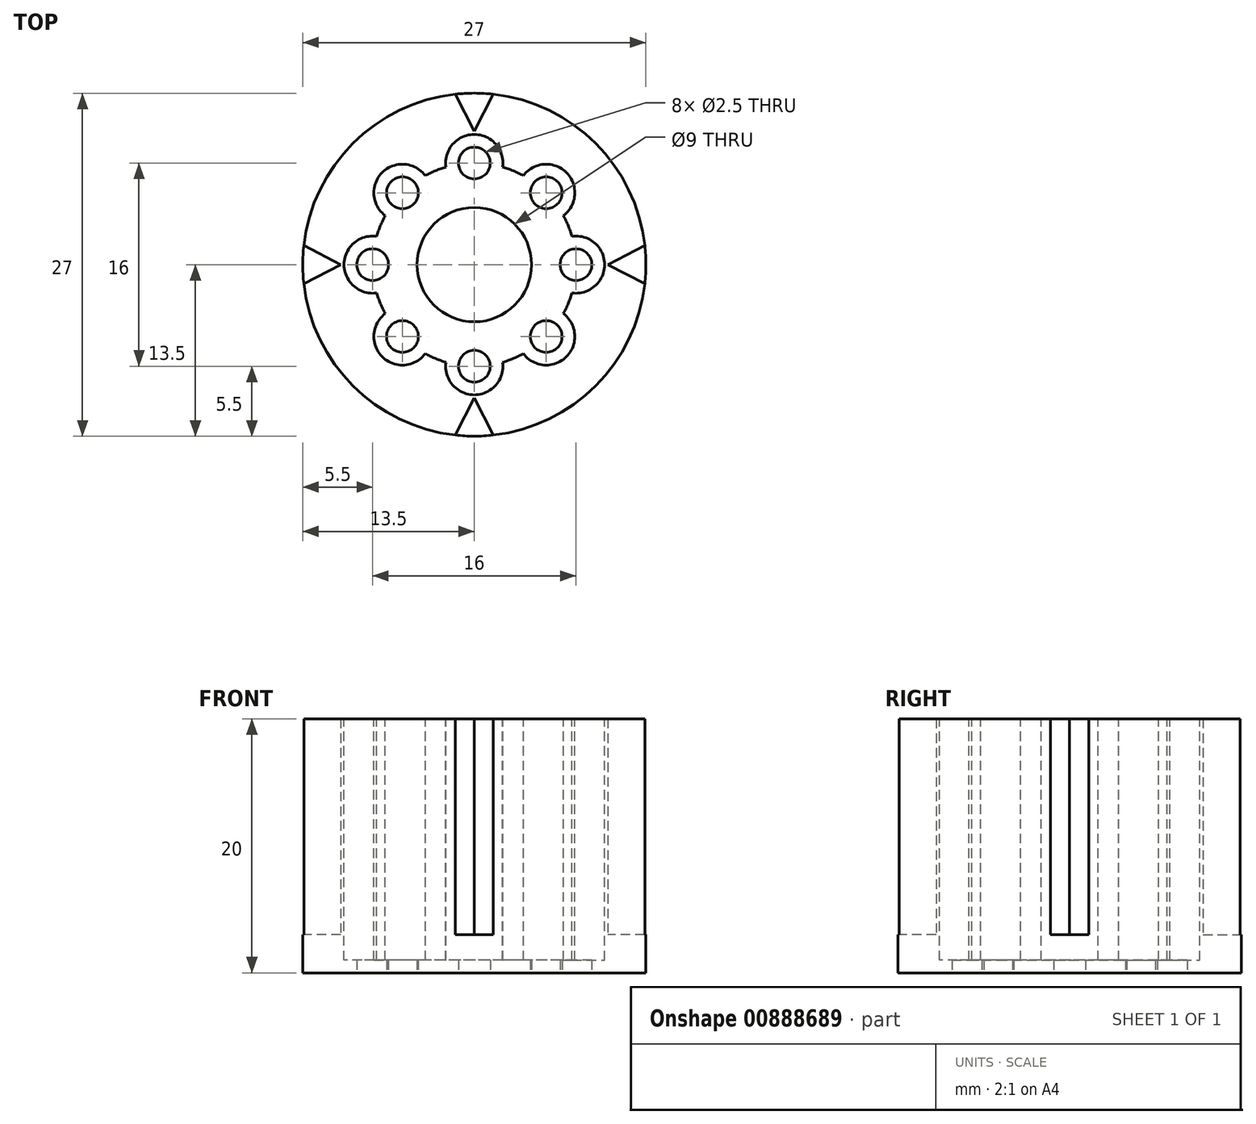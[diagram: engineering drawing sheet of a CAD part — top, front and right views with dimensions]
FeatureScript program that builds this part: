
annotation { "Feature Type Name" : "Feature", "Feature Type Description" : "" }
export const myFeature = defineFeature(function(context is Context, id is Id, definition is map)
    precondition{}
    {
        {
            var Q0;
            Q0=qCreatedBy(makeId("Top.planeOp"),FACE);
            var sketch = newSketch(context, id + "F0", { "sketchPlane" : qUnion([Q0])});
            skArc(sketch, "E0", {"start": v(-13.42, -1.5) * mm, "mid": v(-9.55, -9.55) * mm, "end": v(-1.5, -13.42) * mm});
            skLineSegment(sketch, "E1", {"start": v(-1.5, 13.42) * mm, "end": v(0, 10.5) * mm});
            skLineSegment(sketch, "E2", {"start": v(0, 10.5) * mm, "end": v(1.5, 13.42) * mm});
            skCircle(sketch, "E3", {"center": v(0, 0) * mm, "radius": 10.5 * mm, "construction": true});
            skLineSegment(sketch, "E4", {"start": v(-13.42, 1.5) * mm, "end": v(-10.5, 0) * mm});
            skLineSegment(sketch, "E5", {"start": v(-1.5, -13.42) * mm, "end": v(0, -10.5) * mm});
            skLineSegment(sketch, "E6", {"start": v(13.42, 1.5) * mm, "end": v(10.5, 0) * mm});
            skLineSegment(sketch, "E7", {"start": v(10.5, 0) * mm, "end": v(13.42, -1.5) * mm});
            skLineSegment(sketch, "E8", {"start": v(-10.5, 0) * mm, "end": v(-13.42, -1.5) * mm});
            skLineSegment(sketch, "E9", {"start": v(0, -10.5) * mm, "end": v(1.5, -13.42) * mm});
            skArc(sketch, "E10.trimOffspring", {"start": v(-1.5, 13.42) * mm, "mid": v(-9.55, 9.55) * mm, "end": v(-13.42, 1.5) * mm});
            skArc(sketch, "E11.trimOffspring", {"start": v(13.42, 1.5) * mm, "mid": v(9.55, 9.55) * mm, "end": v(1.5, 13.42) * mm});
            skArc(sketch, "E12.trimOffspring", {"start": v(1.5, -13.42) * mm, "mid": v(9.55, -9.55) * mm, "end": v(13.42, -1.5) * mm});
            skCircle(sketch, "E13", {"center": v(0, 0) * mm, "radius": 4.5 * mm});
            skCircle(sketch, "E14", {"center": v(0, 0) * mm, "radius": 8 * mm, "construction": true});
            skCircle(sketch, "E15", {"center": v(-8, 0) * mm, "radius": 1.25 * mm});
            skCircle(sketch, "E16", {"center": v(0, 8) * mm, "radius": 1.25 * mm});
            skCircle(sketch, "E17", {"center": v(8, 0) * mm, "radius": 1.25 * mm});
            skCircle(sketch, "E18", {"center": v(0, -8) * mm, "radius": 1.25 * mm});
            skCircle(sketch, "E19", {"center": v(-5.66, 5.66) * mm, "radius": 1.25 * mm});
            skCircle(sketch, "E20", {"center": v(5.66, 5.66) * mm, "radius": 1.25 * mm});
            skCircle(sketch, "E21", {"center": v(5.66, -5.66) * mm, "radius": 1.25 * mm});
            skCircle(sketch, "E22", {"center": v(-5.66, -5.66) * mm, "radius": 1.25 * mm});
            skLineSegment(sketch, "E23", {"start": v(-16.79, -16.79) * mm, "end": v(17, 17) * mm, "construction": true});
            skLineSegment(sketch, "E24", {"start": v(-15.4, 15.4) * mm, "end": v(13.72, -13.72) * mm, "construction": true});
            skSolve(sketch);
        }
        {
            var Q0;
            Q0 = qSketchRegion(id + "F0", true);
            extrude(context, id + "F1", {"entities" : qUnion([Q0]), "depth" : 20 * mm, "offsetDistance" : 25 * mm});
        }
        {
            var Q0;
            Q0=makeQuery(id+"F1.opExtrude","CAP_FACE",FACE,{"disambiguationData":[OSD([sQuery(id+"F0.wireOp",EDGE,"E0"),sQuery(id+"F0.wireOp",EDGE,"E1"),sQuery(id+"F0.wireOp",EDGE,"E2"),sQuery(id+"F0.wireOp",EDGE,"E4"),sQuery(id+"F0.wireOp",EDGE,"E5"),sQuery(id+"F0.wireOp",EDGE,"E6"),sQuery(id+"F0.wireOp",EDGE,"E7"),sQuery(id+"F0.wireOp",EDGE,"E8"),sQuery(id+"F0.wireOp",EDGE,"E9"),sQuery(id+"F0.wireOp",EDGE,"E10.trimOffspring"),sQuery(id+"F0.wireOp",EDGE,"E11.trimOffspring"),sQuery(id+"F0.wireOp",EDGE,"E12.trimOffspring"),sQuery(id+"F0.wireOp",EDGE,"E13"),sQuery(id+"F0.wireOp",EDGE,"E15"),sQuery(id+"F0.wireOp",EDGE,"E16"),sQuery(id+"F0.wireOp",EDGE,"E17"),sQuery(id+"F0.wireOp",EDGE,"E18")])],"isStart":false});
            var sketch = newSketch(context, id + "F2", { "sketchPlane" : qUnion([Q0])});
            skArc(sketch, "E25", {"start": v(-7.68, 2.23) * mm, "mid": v(-10.25, 0) * mm, "end": v(-7.68, -2.23) * mm});
            skArc(sketch, "E26", {"start": v(-2.23, -7.68) * mm, "mid": v(0, -10.25) * mm, "end": v(2.23, -7.68) * mm});
            skArc(sketch, "E27", {"start": v(7.68, -2.23) * mm, "mid": v(10.25, 0) * mm, "end": v(7.68, 2.23) * mm});
            skArc(sketch, "E28", {"start": v(2.23, 7.68) * mm, "mid": v(0, 10.25) * mm, "end": v(-2.23, 7.68) * mm});
            skArc(sketch, "E29", {"start": v(-3.86, 7) * mm, "mid": v(-7.25, 7.25) * mm, "end": v(-7, 3.86) * mm});
            skArc(sketch, "E30", {"start": v(3.86, -7) * mm, "mid": v(7.25, -7.25) * mm, "end": v(7, -3.86) * mm});
            skArc(sketch, "E31", {"start": v(-7, -3.86) * mm, "mid": v(-7.25, -7.25) * mm, "end": v(-3.86, -7) * mm});
            skArc(sketch, "E32", {"start": v(7, 3.86) * mm, "mid": v(7.25, 7.25) * mm, "end": v(3.86, 7) * mm});
            skArc(sketch, "E33", {"start": v(-7.68, -2.23) * mm, "mid": v(-7.4, -3.06) * mm, "end": v(-7, -3.86) * mm});
            skArc(sketch, "E34.trimOffspring", {"start": v(-7, 3.86) * mm, "mid": v(-7.4, 3.06) * mm, "end": v(-7.68, 2.23) * mm});
            skArc(sketch, "E35.trimOffspring", {"start": v(-2.23, 7.68) * mm, "mid": v(-3.06, 7.4) * mm, "end": v(-3.86, 7) * mm});
            skArc(sketch, "E36.trimOffspring", {"start": v(3.86, 7) * mm, "mid": v(3.06, 7.4) * mm, "end": v(2.23, 7.68) * mm});
            skArc(sketch, "E37.trimOffspring", {"start": v(7.68, 2.23) * mm, "mid": v(7.4, 3.06) * mm, "end": v(7, 3.86) * mm});
            skArc(sketch, "E38.trimOffspring", {"start": v(7, -3.86) * mm, "mid": v(7.4, -3.06) * mm, "end": v(7.68, -2.23) * mm});
            skArc(sketch, "E39.trimOffspring", {"start": v(2.23, -7.68) * mm, "mid": v(3.06, -7.4) * mm, "end": v(3.86, -7) * mm});
            skArc(sketch, "E40.trimOffspring", {"start": v(-3.86, -7) * mm, "mid": v(-3.06, -7.4) * mm, "end": v(-2.23, -7.68) * mm});
            skSolve(sketch);
        }
        {
            var Q0;
            Q0 = qSketchRegion(id + "F2", true);
            extrude(context, id + "F3", {"entities" : qUnion([Q0]), "operationType" : NewBodyOperationType.REMOVE, "oppositeDirection" : true, "depth" : 19 * mm, "offsetDistance" : 25 * mm});
        }
        {
            var Q0;
            Q0=makeQuery(id+"F1.opExtrude","CAP_FACE",FACE,{"disambiguationData":[OSD([sQuery(id+"F0.wireOp",EDGE,"E0"),sQuery(id+"F0.wireOp",EDGE,"E1"),sQuery(id+"F0.wireOp",EDGE,"E2"),sQuery(id+"F0.wireOp",EDGE,"E4"),sQuery(id+"F0.wireOp",EDGE,"E5"),sQuery(id+"F0.wireOp",EDGE,"E6"),sQuery(id+"F0.wireOp",EDGE,"E7"),sQuery(id+"F0.wireOp",EDGE,"E8"),sQuery(id+"F0.wireOp",EDGE,"E9"),sQuery(id+"F0.wireOp",EDGE,"E10.trimOffspring"),sQuery(id+"F0.wireOp",EDGE,"E11.trimOffspring"),sQuery(id+"F0.wireOp",EDGE,"E12.trimOffspring"),sQuery(id+"F0.wireOp",EDGE,"E13"),sQuery(id+"F0.wireOp",EDGE,"E15"),sQuery(id+"F0.wireOp",EDGE,"E16"),sQuery(id+"F0.wireOp",EDGE,"E17"),sQuery(id+"F0.wireOp",EDGE,"E18"),sQuery(id+"F0.wireOp",EDGE,"E19"),sQuery(id+"F0.wireOp",EDGE,"E20"),sQuery(id+"F0.wireOp",EDGE,"E21"),sQuery(id+"F0.wireOp",EDGE,"E22")])],"isStart":true});
            var sketch = newSketch(context, id + "F4", { "sketchPlane" : qUnion([Q0])});
            skCircle(sketch, "E41", {"center": v(0, 0) * mm, "radius": 13.5 * mm});
            skCircle(sketch, "E42", {"center": v(0, 0) * mm, "radius": 10.5 * mm});
            skSolve(sketch);
        }
        {
            var Q0;
            Q0 = qSketchRegion(id + "F4", true);
            extrude(context, id + "F5", {"entities" : qUnion([Q0]), "operationType" : NewBodyOperationType.ADD, "oppositeDirection" : true, "depth" : 3 * mm, "offsetDistance" : 25 * mm});
        }
    });
